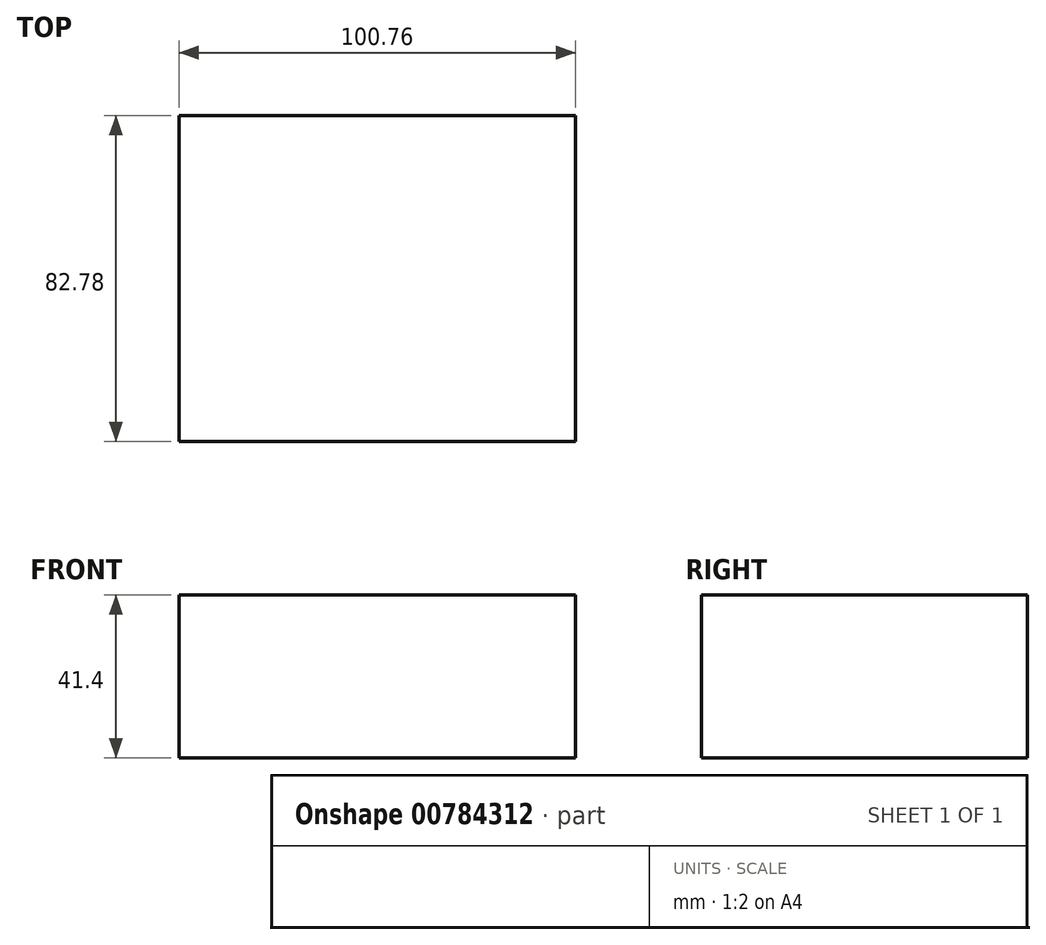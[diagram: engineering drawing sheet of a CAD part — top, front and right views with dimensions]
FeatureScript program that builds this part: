
annotation { "Feature Type Name" : "Feature", "Feature Type Description" : "" }
export const myFeature = defineFeature(function(context is Context, id is Id, definition is map)
    precondition{}
    {
        {
            var Q0;
            Q0=qCreatedBy(makeId("Top.planeOp"),FACE);
            var sketch = newSketch(context, id + "F0", { "sketchPlane" : qUnion([Q0])});
            skLineSegment(sketch, "E0.bottom", {"start": v(-54.49, -49.44) * mm, "end": v(46.27, -49.44) * mm});
            skLineSegment(sketch, "E0.top", {"start": v(-54.49, 33.34) * mm, "end": v(46.27, 33.34) * mm});
            skLineSegment(sketch, "E0.left", {"start": v(-54.49, -49.44) * mm, "end": v(-54.49, 33.34) * mm});
            skLineSegment(sketch, "E0.right", {"start": v(46.27, -49.44) * mm, "end": v(46.27, 33.34) * mm});
            skSolve(sketch);
        }
        {
            var Q0;
            Q0=makeQuery(id+"F0.imprint","IMPRINT",FACE,{"disambiguationData":[TD([[makeQuery(id+"F0.imprint","IMPRINT",EDGE,{"derivedFrom":sQuery(id+"F0.wireOp",EDGE,"E0.bottom")}),1.0]])]});
            extrude(context, id + "F1", {"entities" : qUnion([Q0]), "depth" : 41.4 * mm, "offsetDistance" : 25.4 * mm});
        }
    });
